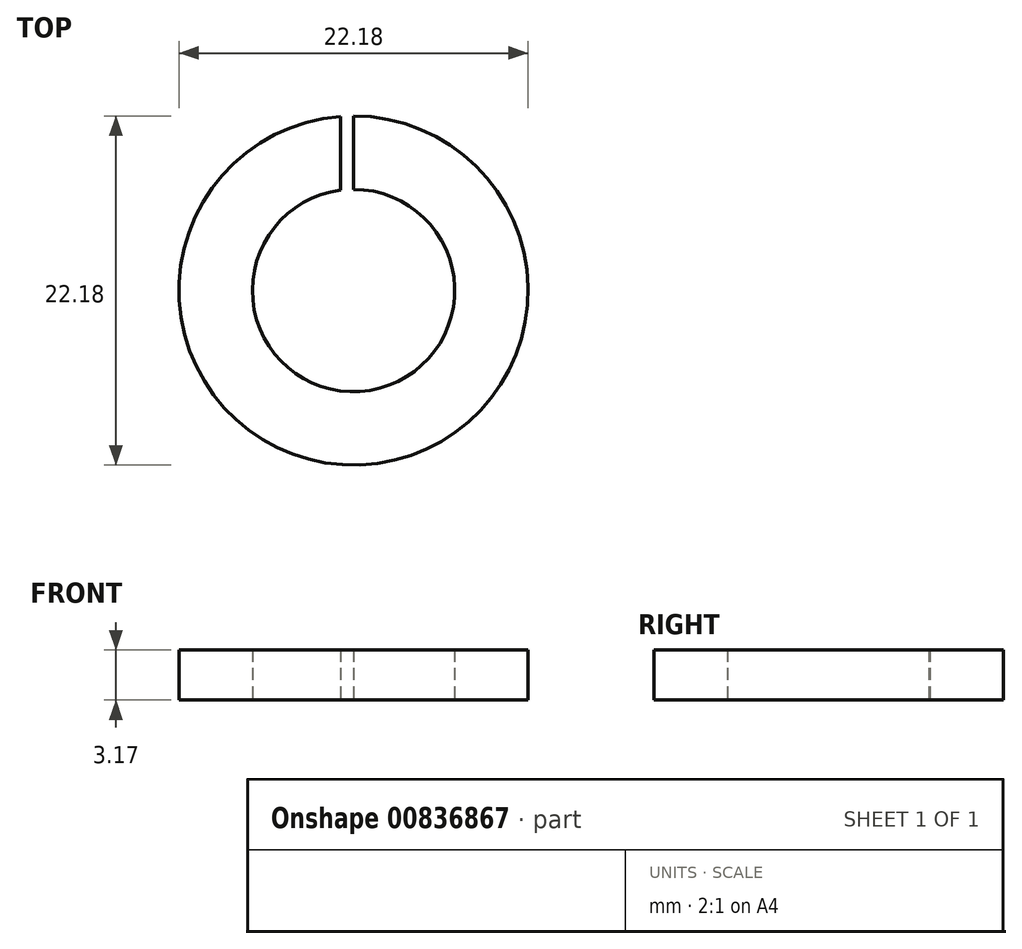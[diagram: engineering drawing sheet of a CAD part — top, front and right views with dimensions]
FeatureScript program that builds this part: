
annotation { "Feature Type Name" : "Feature", "Feature Type Description" : "" }
export const myFeature = defineFeature(function(context is Context, id is Id, definition is map)
    precondition{}
    {
        {
            var Q0;
            Q0=qCreatedBy(makeId("Top.planeOp"),FACE);
            var sketch = newSketch(context, id + "F0", { "sketchPlane" : qUnion([Q0])});
            skArc(sketch, "E0", {"start": v(-0.82, 11.06) * mm, "mid": v(0.41, -11.08) * mm, "end": v(0, 11.09) * mm});
            skArc(sketch, "E1", {"start": v(-0.82, 6.37) * mm, "mid": v(0.41, -6.41) * mm, "end": v(0, 6.43) * mm});
            skLineSegment(sketch, "E2.left", {"start": v(0, 6.43) * mm, "end": v(0, 11.09) * mm});
            skLineSegment(sketch, "E2.right", {"start": v(-0.82, 6.37) * mm, "end": v(-0.82, 11.06) * mm});
            skPoint(sketch, "E2.bottom.start.orphan", {"position": v(0, 2.43) * mm});
            skSolve(sketch);
        }
        {
            var Q0;
            Q0 = qSketchRegion(id + "F0", true);
            extrude(context, id + "F1", {"entities" : qUnion([Q0]), "depth" : 3.17 * mm, "offsetDistance" : 25.4 * mm});
        }
    });
